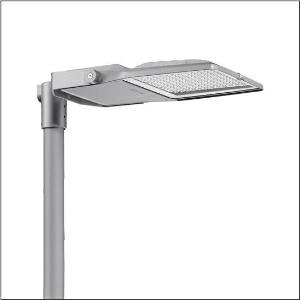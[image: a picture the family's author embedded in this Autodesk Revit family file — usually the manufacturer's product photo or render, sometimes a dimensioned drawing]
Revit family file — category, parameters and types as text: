
# Revit family: floodlight_fl_21_iq_midi___pl52_5xa7782f4d3a_fe87
name_source: partatom
category: Lighting Fixtures
units: mm (PartAtom-declared; Revit-internal decimal feet)

## family parameters
Cut with Voids When Loaded = No
Host = Face
Light Source = No
Part Type = Normal
Room Calculation Point = No
Round Connector Dimension = Use Diameter
Shared = No

## types (1)
- --- (1 x LED, 37330 lm, 270.2 W, 4000K)
    Apparent Load = 270 VA
    CIE Flux Codes = 26 60 98 100 100
    Color Rendering = 70
    Color Temperature = 4000K
    Default Elevation = 1800 mm
    Description = Floodlight FL 21 iQ midi, floodlight, primary light control with lens, of PMMA, primary optical cover: protective disc, of toughened safety glass, transparent, light distribution: PL52, light emission: direct distribution, installation type: surface-mounted, LED, High Power LED, rated luminous flux: 37.330lm, luminous efficacy: 138lm/W, light colour: 740, colour temperature: 4000K, control gear: ECG iQ, control: optimised constant luminous flux control (CLO 2.0), Desk-Remote (wireless, voltage-free reading and setting of iQ features in the workshop via application-optimized NFC function/RFID function), Smart-Wire, Night-Set, Temp-Guard, Auto-Match, Street-Remote, with terminal, 6-pole, mains connection: 220..240V, AC, 50/60Hz, start of lifetime: 270W, end of service life: 287W, reduction: 118W, luminaire housing, of diecast aluminium, powder-coated, Siteco® metallic grey (DB 702S), corrosivity category C5 mid according to DIN EN ISO 12944, sealing non-destructively replaceable, please order mast flange separately, mast bracket, of steel, galvanised, powder-coated, Siteco® metallic grey (DB 702S), protection rating (complete): IP66, insulation class (complete): insulation class II (safety insulation), certification: CE, protection symbol: D, impact resistance: IK08, permissible operating ambient temperature: -40..+40°C, permissible operating ambient temperature for outdoor applications: -40..+50°C, standard: DIN EN 12944, LABS conformity tested according to VDMA 24364:2018-05, packaging unit: 1 piece

Light Distribution: PL52
    Height = 76 mm
    Lamp = 1 x LED
    Lamp Light Flux = 37330 lm
    Lamp Power = 270.2 W
    Lamp count = 1
    Length = 657 mm
    Luminous efficacy = 138 lm/W
    Manufacturer = Siteco
    ModVariant = No
    Model = 5XA7782F4D3A
    Number of Poles = 1
    OnlyDefault = Yes
    Power Factor = 1
    Product Name = Floodlight FL 21 iQ midi | PL52
    Product group = floodlight | pylon annexe
    ProductGroupID = 6200
    Protection Class = Protection class II
    Protection Degree = IP 66
    RLX_Detail_Level = 1
    RLX_Emergency_Light_Flux = 0 lm
    RLX_Emergency_Type = 0
    RLX_Emergency_Type_DB = No
    RlxData = <blob elided: 153749 chars, md5=0d73d08b>
    Socket = socket
    Standby Power = 0 W
    System Light Flux = 37330 lm
    System Power = 270 W
    Type Comments = factory setting: luminous flux: 100 % | dim-lin: 254 | 620 mA
    Type Image = l_1007123.jpg
    URL = http://relux.com
    VarID = @adj_053807
    Voltage = 0 V
    Weight = 0.00 kg
    Width = 442 mm

## geometry (parser evidence)
native form markers: Blend x4, Sweep x14
no freeform markers — native parametric forms only
